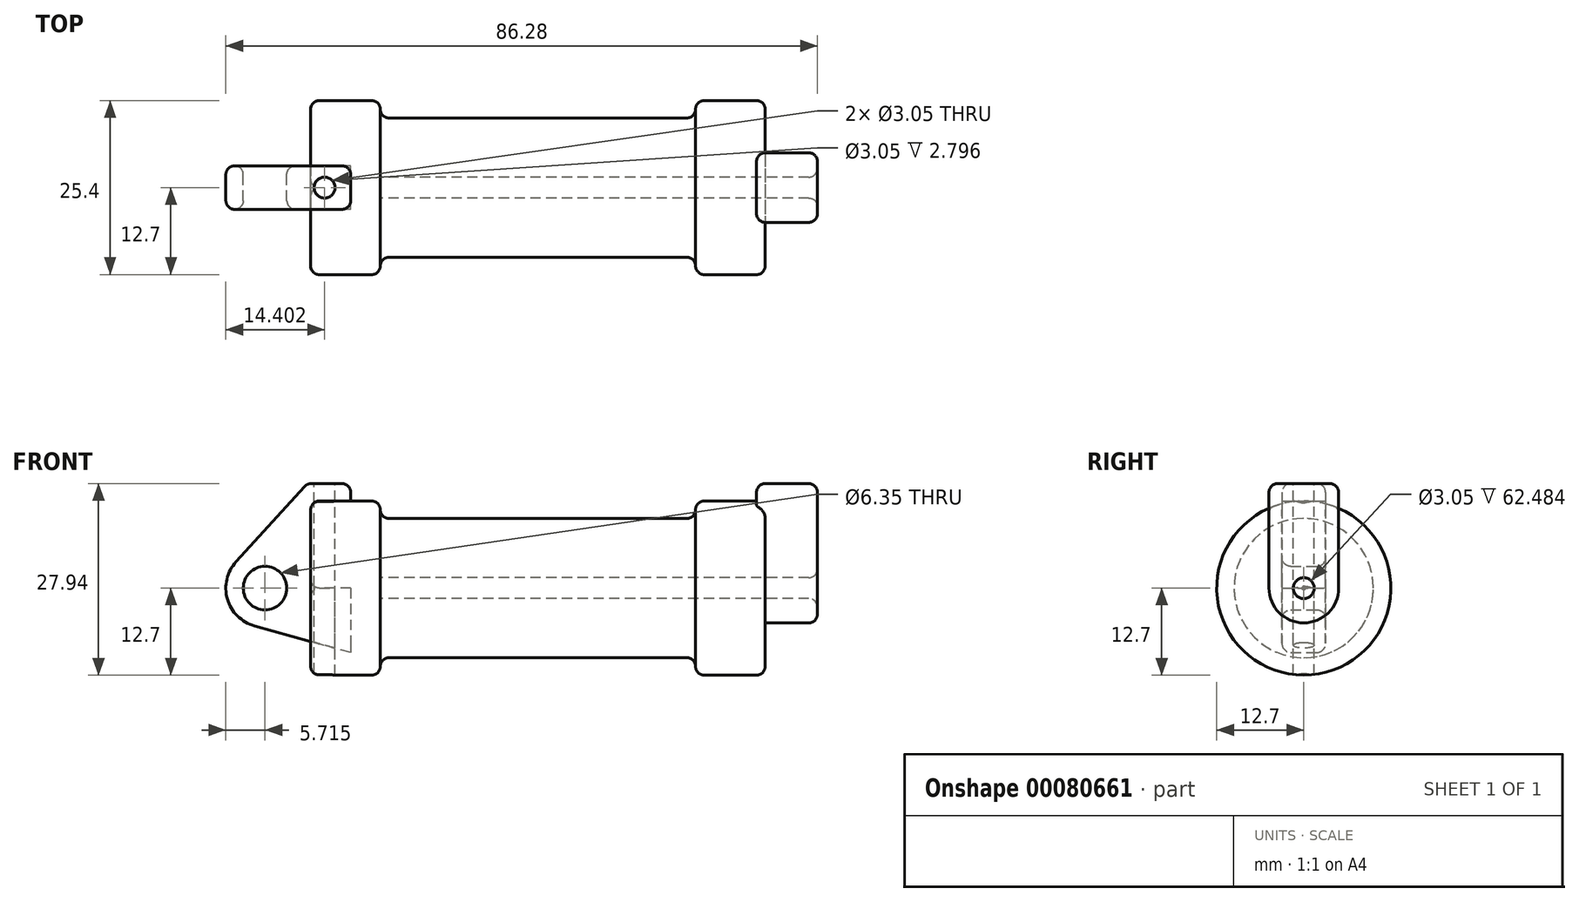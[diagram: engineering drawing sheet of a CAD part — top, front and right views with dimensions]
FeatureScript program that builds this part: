
annotation { "Feature Type Name" : "Feature", "Feature Type Description" : "" }
export const myFeature = defineFeature(function(context is Context, id is Id, definition is map)
    precondition{}
    {
        {
            var Q0;
            Q0=qCreatedBy(makeId("Front.planeOp"),FACE);
            var sketch = newSketch(context, id + "F0", { "sketchPlane" : qUnion([Q0])});
            skLineSegment(sketch, "E0", {"start": v(0, 1.27) * mm, "end": v(0, 11.43) * mm});
            skLineSegment(sketch, "E1", {"start": v(1.27, 12.7) * mm, "end": v(8.9, 12.7) * mm});
            skLineSegment(sketch, "E2", {"start": v(10.16, 11.43) * mm, "end": v(10.16, 10.16) * mm});
            skLineSegment(sketch, "E3", {"start": v(10.16, 10.16) * mm, "end": v(56.13, 10.16) * mm});
            skLineSegment(sketch, "E4", {"start": v(56.13, 10.16) * mm, "end": v(56.13, 12.7) * mm});
            skLineSegment(sketch, "E5", {"start": v(56.13, 12.7) * mm, "end": v(66.3, 12.7) * mm});
            skLineSegment(sketch, "E6", {"start": v(66.3, 12.7) * mm, "end": v(66.3, 0) * mm});
            skLineSegment(sketch, "E7", {"start": v(66.3, 0) * mm, "end": v(1.27, 0) * mm});
            skLineSegment(sketch, "E8", {"start": v(4.57, 15.24) * mm, "end": v(-0.5, 15.24) * mm});
            skLineSegment(sketch, "E9", {"start": v(-0.5, 15.24) * mm, "end": v(-10.88, 3.85) * mm});
            skLineSegment(sketch, "E10", {"start": v(0, 0) * mm, "end": v(-6.65, 0) * mm});
            skCircle(sketch, "E11", {"center": v(-6.65, 0) * mm, "radius": 5.72 * mm});
            skCircle(sketch, "E12", {"center": v(-6.65, 0) * mm, "radius": 3.18 * mm});
            skLineSegment(sketch, "E13", {"start": v(5.84, 13.97) * mm, "end": v(5.84, -9.4) * mm});
            skLineSegment(sketch, "E14", {"start": v(5.84, -9.4) * mm, "end": v(-8.18, -5.5) * mm});
            skPoint(sketch, "E15.visualSharp", {"position": v(10.16, 12.7) * mm});
            skArc(sketch, "E15.filletArc", {"start": v(10.16, 11.43) * mm, "mid": v(9.79, 12.33) * mm, "end": v(8.9, 12.7) * mm});
            skPoint(sketch, "E16.visualSharp", {"position": v(5.84, 15.24) * mm});
            skArc(sketch, "E16.filletArc", {"start": v(5.84, 13.97) * mm, "mid": v(5.47, 14.87) * mm, "end": v(4.57, 15.24) * mm});
            skPoint(sketch, "E17.visualSharp", {"position": v(0, 12.7) * mm});
            skArc(sketch, "E17.filletArc", {"start": v(1.27, 12.7) * mm, "mid": v(0.37, 12.33) * mm, "end": v(0, 11.43) * mm});
            skPoint(sketch, "E18.visualSharp", {"position": v(0, 0) * mm});
            skArc(sketch, "E18.filletArc", {"start": v(0, 1.27) * mm, "mid": v(0.37, 0.37) * mm, "end": v(1.27, 0) * mm});
            skSolve(sketch);
        }
        {
            var Q0;
            {var subQ0=sQuery(id+"F0.wireOp",EDGE,"E2");Q0=makeQuery(id+"F0.imprint","IMPRINT",FACE,{"disambiguationData":[TD([[makeQuery(id+"F0.imprint","IMPRINT",EDGE,{"derivedFrom":subQ0}),-1.0]])]});}
            var Q1;
            {var subQ0=sQuery(id+"F0.wireOp",EDGE,"E0");Q1=makeQuery(id+"F0.imprint","IMPRINT",FACE,{"disambiguationData":[TD([[makeQuery(id+"F0.imprint","IMPRINT",EDGE,{"derivedFrom":subQ0}),-1.0]])]});}
            var Q2;
            Q2=sQuery(id+"F0.wireOp",EDGE,"E7");
            revolve(context, id + "F1", {"entities" : qUnion([Q0, Q1]), "axis" : qUnion([Q2]), "revolveType" : RevolveType.FULL});
        }
        {
            var Q0;
            {var subQ3=sQuery(id+"F0.wireOp",EDGE,"E0");Q0=makeQuery(id+"F0.imprint","IMPRINT",FACE,{"disambiguationData":[TD([[makeQuery(id+"F0.imprint","IMPRINT",EDGE,{"derivedFrom":subQ3}),1.0]])]});}
            var Q1;
            {var subQ0=sQuery(id+"F0.wireOp",EDGE,"E14");Q1=makeQuery(id+"F0.imprint","IMPRINT",FACE,{"disambiguationData":[TD([[makeQuery(id+"F0.imprint","IMPRINT",EDGE,{"derivedFrom":subQ0}),-1.0]])]});}
            var Q2;
            {var subQ4=sQuery(id+"F0.wireOp",EDGE,"E12");Q2=makeQuery(id+"F0.imprint","IMPRINT",FACE,{"disambiguationData":[TD([[makeQuery(id+"F0.imprint","IMPRINT",EDGE,{"derivedFrom":subQ4}),-1.0]])]});}
            extrude(context, id + "F2", {"entities" : qUnion([Q0, Q1, Q2]), "endBound" : BoundingType.SYMMETRIC, "depth" : 6.35 * mm});
        }
        {
            var Q0;
            Q0=makeQuery(id+"F1.opRevolve","SWEPT_FACE",FACE,{"disambiguationData":[OSD([sQuery(id+"F0.wireOp",EDGE,"E6")])]});
            var sketch = newSketch(context, id + "F3", { "sketchPlane" : qUnion([Q0])});
            skCircle(sketch, "E19", {"center": v(0, 0) * mm, "radius": 5.08 * mm});
            skCircle(sketch, "E20", {"center": v(0, 0) * mm, "radius": 1.52 * mm});
            skLineSegment(sketch, "E21", {"start": v(-5.08, 0) * mm, "end": v(-5.08, 13.97) * mm});
            skLineSegment(sketch, "E22", {"start": v(5.08, 0) * mm, "end": v(5.08, 13.97) * mm});
            skLineSegment(sketch, "E23", {"start": v(3.81, 15.24) * mm, "end": v(-3.81, 15.24) * mm});
            skPoint(sketch, "E24.visualSharp", {"position": v(-5.08, 15.24) * mm});
            skArc(sketch, "E24.filletArc", {"start": v(-3.81, 15.24) * mm, "mid": v(-4.7, 14.87) * mm, "end": v(-5.08, 13.97) * mm});
            skPoint(sketch, "E25.visualSharp", {"position": v(5.08, 15.24) * mm});
            skArc(sketch, "E25.filletArc", {"start": v(5.08, 13.97) * mm, "mid": v(4.7, 14.87) * mm, "end": v(3.81, 15.24) * mm});
            skSolve(sketch);
        }
        {
            var Q0;
            Q0 = qSketchRegion(id + "F3", true);
            extrude(context, id + "F4", {"entities" : qUnion([Q0]), "operationType" : NewBodyOperationType.ADD, "depth" : 7.62 * mm, "hasSecondDirection" : true, "secondDirectionOppositeDirection" : true, "secondDirectionDepth" : 1.27 * mm});
        }
        {
            var Q0;
            Q0=makeQuery(id+"F2.opExtrude","SWEPT_FACE",FACE,{"disambiguationData":[OSD([sQuery(id+"F0.wireOp",EDGE,"E8")])]});
            var sketch = newSketch(context, id + "F5", { "sketchPlane" : qUnion([Q0])});
            skCircle(sketch, "E26", {"center": v(2.03, 0) * mm, "radius": 1.52 * mm});
            skPoint(sketch, "E26.centerSnap0", {"position": v(2.03, 3.18) * mm});
            skSolve(sketch);
        }
        {
            var Q0;
            Q0=makeQuery(id+"F5.imprint","IMPRINT",FACE,{"disambiguationData":[TD([[makeQuery(id+"F5.imprint","IMPRINT",EDGE,{"derivedFrom":sQuery(id+"F5.wireOp",EDGE,"E26")}),1.0]])]});
            extrude(context, id + "F6", {"entities" : qUnion([Q0]), "operationType" : NewBodyOperationType.REMOVE, "endBound" : BoundingType.THROUGH_ALL, "oppositeDirection" : true, "depth" : 12.7 * mm});
        }
        {
            var Q0;
            Q0=makeQuery(id+"F4.boolean.opBoolean","SPLIT",FACE,{"disambiguationData":[TD([makeQuery(id+"F4.opExtrude","SWEPT_FACE",FACE,{"disambiguationData":[OSD([sQuery(id+"F3.wireOp",EDGE,"E20")])]})])],"derivedFrom":makeQuery(id+"F1.opRevolve","SWEPT_FACE",FACE,{"disambiguationData":[OSD([sQuery(id+"F0.wireOp",EDGE,"E6")])]})});
            var Q1;
            Q1=makeQuery(id+"F1.opRevolve","SWEPT_FACE",FACE,{"disambiguationData":[OSD([sQuery(id+"F0.wireOp",EDGE,"E2")])]});
            extrude(context, id + "F7", {"entities" : qUnion([Q0]), "operationType" : NewBodyOperationType.REMOVE, "endBound" : BoundingType.UP_TO_SURFACE, "oppositeDirection" : true, "endBoundEntityFace" : qUnion([Q1]), "depth" : 25.4 * mm, "hasSecondDirection" : true, "secondDirectionBound" : SecondDirectionBoundingType.THROUGH_ALL, "secondDirectionOppositeDirection" : false, "secondDirectionDepth" : 25.4 * mm});
        }
        {
            var Q0;
            Q0=makeQuery(id+"F2.opExtrude","SWEPT_EDGE",EDGE,{"disambiguationData":[OSD([sQuery(id+"F0.wireOp",EDGE,"E8"),sQuery(id+"F0.wireOp",EDGE,"E9")])]});
            fillet(context, id + "F8", {"entities" : qUnion([Q0]), "radius" : 1.27 * mm, "tangentPropagation" : true, "allowEdgeOverflow" : false});
        }
        {
            var Q0;
            Q0=makeQuery(id+"F1.opRevolve","SWEPT_EDGE",EDGE,{"disambiguationData":[OSD([sQuery(id+"F0.wireOp",EDGE,"E4"),sQuery(id+"F0.wireOp",EDGE,"E5")])]});
            fillet(context, id + "F9", {"entities" : qUnion([Q0]), "radius" : 1.27 * mm, "tangentPropagation" : true, "allowEdgeOverflow" : false});
        }
        {
            var Q0;
            Q0=makeQuery(id+"F4.opExtrude","CAP_EDGE",EDGE,{"disambiguationData":[OSD([sQuery(id+"F3.wireOp",EDGE,"E23")])],"isStart":true});
            fillet(context, id + "F10", {"entities" : qUnion([Q0]), "radius" : 1.27 * mm, "tangentPropagation" : true, "allowEdgeOverflow" : false});
        }
        {
            var Q0;
            Q0=makeQuery(id+"F1.opRevolve","SWEPT_EDGE",EDGE,{"disambiguationData":[OSD([sQuery(id+"F0.wireOp",EDGE,"E3"),sQuery(id+"F0.wireOp",EDGE,"E4")])]});
            fillet(context, id + "F11", {"entities" : qUnion([Q0]), "radius" : 1.27 * mm, "tangentPropagation" : true, "allowEdgeOverflow" : false});
        }
        {
            var Q0;
            Q0=makeQuery(id+"F2.opExtrude","CAP_EDGE",EDGE,{"disambiguationData":[OSD([sQuery(id+"F0.wireOp",EDGE,"E9")])],"isStart":true});
            fillet(context, id + "F12", {"entities" : qUnion([Q0]), "radius" : 1.27 * mm, "tangentPropagation" : true, "allowEdgeOverflow" : false});
        }
        {
            var Q0;
            Q0=makeQuery(id+"F2.opExtrude","CAP_EDGE",EDGE,{"disambiguationData":[OSD([sQuery(id+"F0.wireOp",EDGE,"E12")])],"isStart":true});
            fillet(context, id + "F13", {"entities" : qUnion([Q0]), "radius" : 1.27 * mm, "tangentPropagation" : true, "allowEdgeOverflow" : false});
        }
        {
            var Q0;
            Q0=makeQuery(id+"F2.opExtrude","CAP_EDGE",EDGE,{"disambiguationData":[OSD([sQuery(id+"F0.wireOp",EDGE,"E12")])],"isStart":false});
            fillet(context, id + "F14", {"entities" : qUnion([Q0]), "radius" : 1.27 * mm, "tangentPropagation" : true, "allowEdgeOverflow" : false});
        }
        {
            var Q0;
            Q0=makeQuery(id+"F1.opRevolve","SWEPT_EDGE",EDGE,{"disambiguationData":[OSD([sQuery(id+"F0.wireOp",EDGE,"E2"),sQuery(id+"F0.wireOp",EDGE,"E3")])]});
            var Q1;
            Q1=makeQuery(id+"F1.opRevolve","SWEPT_EDGE",EDGE,{"disambiguationData":[OSD([sQuery(id+"F0.wireOp",EDGE,"E5"),sQuery(id+"F0.wireOp",EDGE,"E6")])]});
            var Q2;
            Q2=makeQuery(id+"F4.opExtrude","CAP_EDGE",EDGE,{"disambiguationData":[OSD([sQuery(id+"F3.wireOp",EDGE,"E21")])],"isStart":false});
            var Q3;
            Q3=makeQuery(id+"F4.opExtrude","CAP_EDGE",EDGE,{"disambiguationData":[OSD([sQuery(id+"F3.wireOp",EDGE,"E20")])],"isStart":false});
            var Q4;
            Q4=makeQuery(id+"F4.opExtrude","SWEPT_EDGE",EDGE,{"disambiguationData":[OSD([sQuery(id+"F3.wireOp",EDGE,"E19"),sQuery(id+"F3.wireOp",EDGE,"E21")])]});
            fillet(context, id + "F15", {"entities" : qUnion([Q0, Q1, Q2, Q3, Q4]), "radius" : 1.27 * mm, "tangentPropagation" : true, "allowEdgeOverflow" : false});
        }
        {
            var Q0;
            Q0=makeQuery(id+"F2.opExtrude","CAP_EDGE",EDGE,{"disambiguationData":[OSD([sQuery(id+"F0.wireOp",EDGE,"E8")])],"isStart":false});
            var Q1;
            Q1=makeQuery(id+"F2.opExtrude","CAP_EDGE",EDGE,{"disambiguationData":[OSD([sQuery(id+"F0.wireOp",EDGE,"E9")])],"isStart":false});
            fillet(context, id + "F16", {"entities" : qUnion([Q0, Q1]), "radius" : 1.27 * mm, "tangentPropagation" : true, "allowEdgeOverflow" : false});
        }
    });
